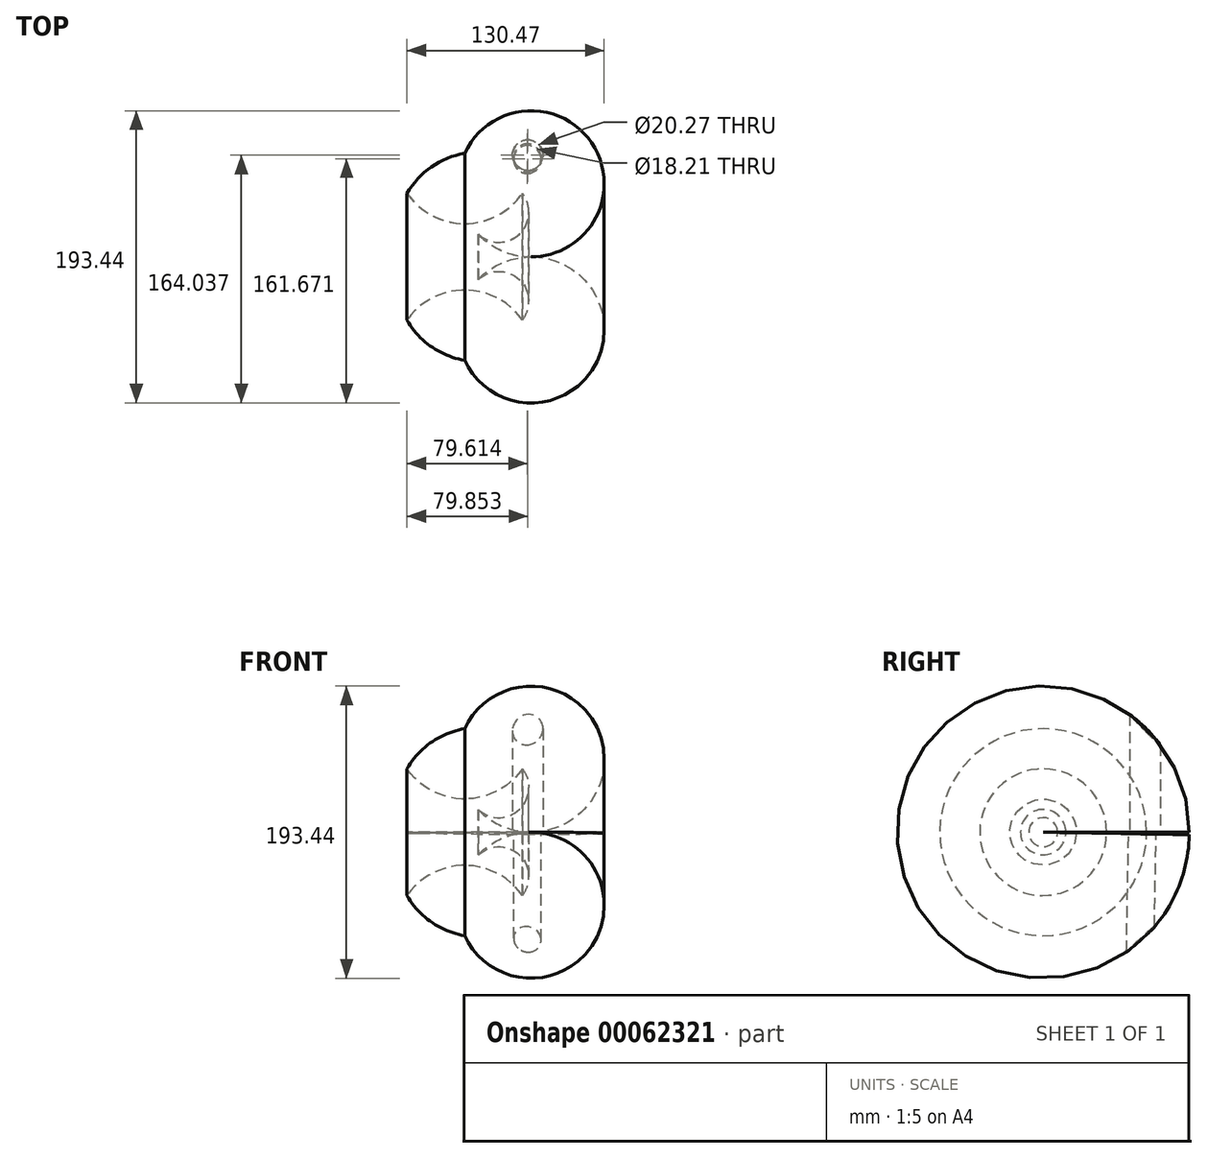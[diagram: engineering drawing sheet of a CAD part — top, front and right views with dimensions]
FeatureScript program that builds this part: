
annotation { "Feature Type Name" : "Feature", "Feature Type Description" : "" }
export const myFeature = defineFeature(function(context is Context, id is Id, definition is map)
    precondition{}
    {
        {
            var Q0;
            Q0=qCreatedBy(makeId("Top.planeOp"),FACE);
            var sketch = newSketch(context, id + "F0", { "sketchPlane" : qUnion([Q0])});
            skArc(sketch, "E0", {"start": v(-76.28, 0) * mm, "mid": v(-38.14, -19.9) * mm, "end": v(0, 0) * mm});
            skArc(sketch, "E1", {"start": v(-38.14, 26.57) * mm, "mid": v(-60.2, 17.58) * mm, "end": v(-76.28, 0) * mm});
            skArc(sketch, "E2", {"start": v(-29.22, -26.88) * mm, "mid": v(53.53, 14.4) * mm, "end": v(-38.14, 26.57) * mm});
            skArc(sketch, "E3", {"start": v(-29.22, -26.88) * mm, "mid": v(-2.1, -27.04) * mm, "end": v(0, 0) * mm});
            skLineSegment(sketch, "E4", {"start": v(5.83, -41.92) * mm, "end": v(75.72, -41.92) * mm});
            skSolve(sketch);
        }
        {
            var Q0;
            Q0=makeQuery(id+"F0.imprint","IMPRINT",FACE,{"disambiguationData":[TD([[makeQuery(id+"F0.imprint","IMPRINT",EDGE,{"derivedFrom":sQuery(id+"F0.wireOp",EDGE,"E0")}),1.0]])]});
            var Q1;
            Q1=sQuery(id+"F0.wireOp",EDGE,"E4");
            revolve(context, id + "F1", {"entities" : qUnion([Q0]), "axis" : qUnion([Q1]), "revolveType" : RevolveType.ONE_DIRECTION, "angle" : 359 * degree});
        }
        {
            var Q0;
            Q0=makeQuery(id+"F1.opRevolve","CAP_FACE",FACE,{"disambiguationData":[OSD([sQuery(id+"F0.wireOp",EDGE,"E0"),sQuery(id+"F0.wireOp",EDGE,"E1"),sQuery(id+"F0.wireOp",EDGE,"E2"),sQuery(id+"F0.wireOp",EDGE,"E3")])],"isStart":true});
            var sketch = newSketch(context, id + "F2", { "sketchPlane" : qUnion([Q0])});
            skCircle(sketch, "E5", {"center": v(3.57, -25.4) * mm, "radius": 10.13 * mm});
            skSolve(sketch);
        }
        {
            var Q0;
            Q0 = qSketchRegion(id + "F2", true);
            extrude(context, id + "F3", {"entities" : qUnion([Q0]), "operationType" : NewBodyOperationType.REMOVE, "oppositeDirection" : true, "depth" : 103.12 * mm});
        }
        {
            var Q0;
            Q0=makeQuery(id+"F1.opRevolve","CAP_FACE",FACE,{"disambiguationData":[OSD([sQuery(id+"F0.wireOp",EDGE,"E0"),sQuery(id+"F0.wireOp",EDGE,"E1"),sQuery(id+"F0.wireOp",EDGE,"E2"),sQuery(id+"F0.wireOp",EDGE,"E3")])],"isStart":false});
            var sketch = newSketch(context, id + "F4", { "sketchPlane" : qUnion([Q0])});
            skCircle(sketch, "E6", {"center": v(3.33, 23.73) * mm, "radius": 9.1 * mm});
            skSolve(sketch);
        }
        {
            var Q0;
            Q0 = qSketchRegion(id + "F4", true);
            extrude(context, id + "F5", {"entities" : qUnion([Q0]), "operationType" : NewBodyOperationType.REMOVE, "oppositeDirection" : true, "depth" : 130.56 * mm});
        }
    });
